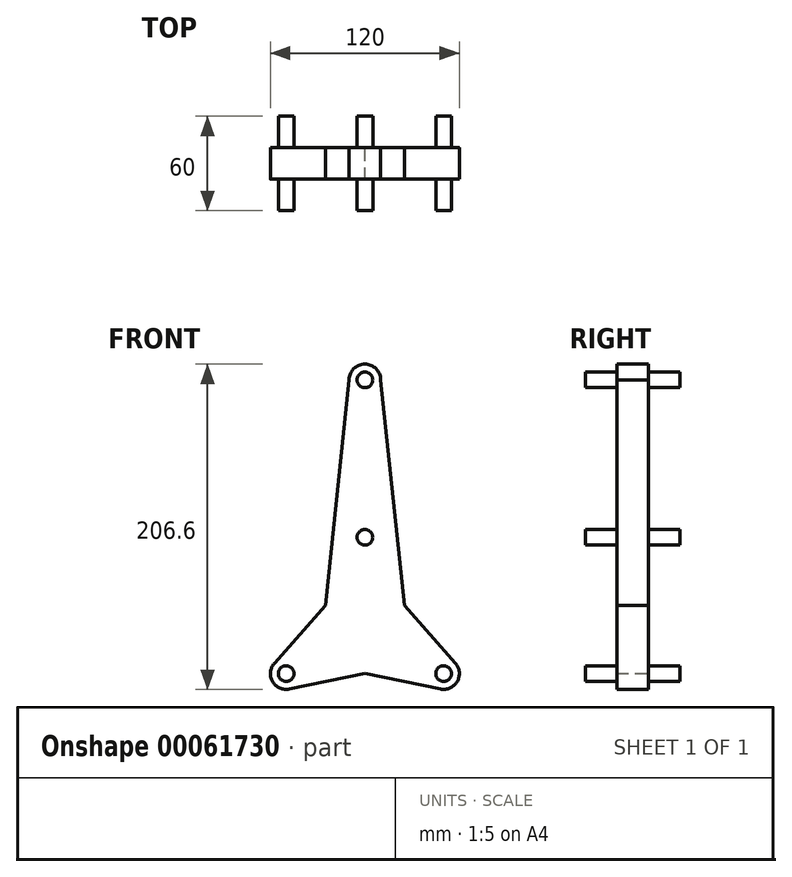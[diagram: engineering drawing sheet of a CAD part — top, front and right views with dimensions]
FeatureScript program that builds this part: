
annotation { "Feature Type Name" : "Feature", "Feature Type Description" : "" }
export const myFeature = defineFeature(function(context is Context, id is Id, definition is map)
    precondition{}
    {
        {
            var Q0;
            Q0=qCreatedBy(makeId("Front.planeOp"),FACE);
            var sketch = newSketch(context, id + "F0", { "sketchPlane" : qUnion([Q0])});
            skLineSegment(sketch, "E0", {"start": v(0, 0) * mm, "end": v(-50, -86.6) * mm});
            skLineSegment(sketch, "E1", {"start": v(-50, -86.6) * mm, "end": v(50, -86.6) * mm});
            skLineSegment(sketch, "E2", {"start": v(50, -86.6) * mm, "end": v(0, 0) * mm});
            skCircle(sketch, "E3", {"center": v(-50, -86.6) * mm, "radius": 5 * mm});
            skCircle(sketch, "E4", {"center": v(-50, -86.6) * mm, "radius": 10 * mm});
            skCircle(sketch, "E5", {"center": v(50, -86.6) * mm, "radius": 5 * mm});
            skCircle(sketch, "E6", {"center": v(50, -86.6) * mm, "radius": 10 * mm});
            skCircle(sketch, "E7", {"center": v(0, 0) * mm, "radius": 5 * mm});
            skCircle(sketch, "E8", {"center": v(0, 0) * mm, "radius": 10 * mm});
            skCircle(sketch, "E9", {"center": v(0, 100) * mm, "radius": 5 * mm});
            skCircle(sketch, "E10", {"center": v(0, 100) * mm, "radius": 10 * mm});
            skLineSegment(sketch, "E11", {"start": v(-25, -43.3) * mm, "end": v(-10, 100) * mm});
            skLineSegment(sketch, "E12", {"start": v(25, -43.3) * mm, "end": v(10, 100) * mm});
            skLineSegment(sketch, "E13", {"start": v(-25, -43.3) * mm, "end": v(-57.49, -79.97) * mm});
            skLineSegment(sketch, "E14", {"start": v(25, -43.3) * mm, "end": v(57.49, -79.97) * mm});
            skLineSegment(sketch, "E15", {"start": v(0, -86.6) * mm, "end": v(-48, -96.4) * mm});
            skLineSegment(sketch, "E16", {"start": v(0, -86.6) * mm, "end": v(48, -96.4) * mm});
            skSolve(sketch);
        }
        {
            var Q0;
            {var subQ0=sQuery(id+"F0.wireOp",EDGE,"E11");Q0=makeQuery(id+"F0.imprint","IMPRINT",FACE,{"disambiguationData":[TD([[makeQuery(id+"F0.imprint","IMPRINT",EDGE,{"derivedFrom":subQ0}),-1.0]])]});}
            var Q1;
            {var subQ0=sQuery(id+"F0.wireOp",EDGE,"E6");var subQ1=sQuery(id+"F0.wireOp",EDGE,"E1");var subQ2=makeQuery(id+"F0.imprint","INTERSECT",VERTEX,{"derivedFrom":[subQ1,subQ0]});Q1=makeQuery(id+"F0.imprint","IMPRINT",FACE,{"disambiguationData":[TD([[makeQuery(id+"F0.imprint","IMPRINT",EDGE,{"disambiguationData":[TD([[subQ2,-1.0]])],"derivedFrom":subQ1}),1.0]])]});}
            var Q2;
            {var subQ0=sQuery(id+"F0.wireOp",EDGE,"E7");var subQ1=sQuery(id+"F0.wireOp",EDGE,"E0");var subQ2=makeQuery(id+"F0.imprint","INTERSECT",VERTEX,{"derivedFrom":[subQ1,subQ0]});Q2=makeQuery(id+"F0.imprint","IMPRINT",FACE,{"disambiguationData":[TD([[makeQuery(id+"F0.imprint","IMPRINT",EDGE,{"disambiguationData":[TD([[subQ2,-1.0]])],"derivedFrom":subQ1}),-1.0]])]});}
            var Q3;
            {var subQ0=sQuery(id+"F0.wireOp",EDGE,"E13");Q3=makeQuery(id+"F0.imprint","IMPRINT",FACE,{"disambiguationData":[TD([[makeQuery(id+"F0.imprint","IMPRINT",EDGE,{"derivedFrom":subQ0}),1.0]])]});}
            var Q4;
            {var subQ3=sQuery(id+"F0.wireOp",EDGE,"E6");var subQ6=sQuery(id+"F0.wireOp",EDGE,"E1");var subQ8=makeQuery(id+"F0.imprint","INTERSECT",VERTEX,{"derivedFrom":[subQ6,subQ3]});Q4=makeQuery(id+"F0.imprint","IMPRINT",FACE,{"disambiguationData":[TD([[makeQuery(id+"F0.imprint","IMPRINT",EDGE,{"disambiguationData":[TD([[subQ8,-1.0]])],"derivedFrom":subQ6}),-1.0]])]});}
            var Q5;
            {var subQ0=sQuery(id+"F0.wireOp",EDGE,"E4");var subQ1=sQuery(id+"F0.wireOp",EDGE,"E0");var subQ2=makeQuery(id+"F0.imprint","INTERSECT",VERTEX,{"derivedFrom":[subQ1,subQ0]});Q5=makeQuery(id+"F0.imprint","IMPRINT",FACE,{"disambiguationData":[TD([[makeQuery(id+"F0.imprint","IMPRINT",EDGE,{"disambiguationData":[TD([[subQ2,-1.0]])],"derivedFrom":subQ1}),1.0]])]});}
            var Q6;
            {var subQ0=sQuery(id+"F0.wireOp",EDGE,"E15");Q6=makeQuery(id+"F0.imprint","IMPRINT",FACE,{"disambiguationData":[TD([[makeQuery(id+"F0.imprint","IMPRINT",EDGE,{"derivedFrom":subQ0}),-1.0]])]});}
            var Q7;
            {var subQ0=sQuery(id+"F0.wireOp",EDGE,"E16");Q7=makeQuery(id+"F0.imprint","IMPRINT",FACE,{"disambiguationData":[TD([[makeQuery(id+"F0.imprint","IMPRINT",EDGE,{"derivedFrom":subQ0}),1.0]])]});}
            var Q8;
            {var subQ0=sQuery(id+"F0.wireOp",EDGE,"E14");Q8=makeQuery(id+"F0.imprint","IMPRINT",FACE,{"disambiguationData":[TD([[makeQuery(id+"F0.imprint","IMPRINT",EDGE,{"derivedFrom":subQ0}),-1.0]])]});}
            var Q9;
            Q9=makeQuery(id+"F0.imprint","IMPRINT",FACE,{"disambiguationData":[TD([[makeQuery(id+"F0.imprint","IMPRINT",EDGE,{"derivedFrom":sQuery(id+"F0.wireOp",EDGE,"E9")}),-1.0]])]});
            var Q10;
            {var subQ0=sQuery(id+"F0.wireOp",EDGE,"E4");var subQ2=sQuery(id+"F0.wireOp",EDGE,"E0");var subQ3=makeQuery(id+"F0.imprint","INTERSECT",VERTEX,{"derivedFrom":[subQ2,subQ0]});Q10=makeQuery(id+"F0.imprint","IMPRINT",FACE,{"disambiguationData":[TD([[makeQuery(id+"F0.imprint","IMPRINT",EDGE,{"disambiguationData":[TD([[subQ3,-1.0]])],"derivedFrom":subQ2}),-1.0]])]});}
            var Q11;
            {var subQ4=sQuery(id+"F0.wireOp",EDGE,"E0");var subQ8=sQuery(id+"F0.wireOp",EDGE,"E4");var subQ12=makeQuery(id+"F0.imprint","INTERSECT",VERTEX,{"derivedFrom":[subQ4,subQ8]});Q11=makeQuery(id+"F0.imprint","IMPRINT",FACE,{"disambiguationData":[TD([[makeQuery(id+"F0.imprint","IMPRINT",EDGE,{"disambiguationData":[TD([[subQ12,1.0]])],"derivedFrom":subQ8}),-1.0]])]});}
            var Q12;
            {var subQ0=sQuery(id+"F0.wireOp",EDGE,"E7");var subQ1=sQuery(id+"F0.wireOp",EDGE,"E0");var subQ2=makeQuery(id+"F0.imprint","INTERSECT",VERTEX,{"derivedFrom":[subQ1,subQ0]});Q12=makeQuery(id+"F0.imprint","IMPRINT",FACE,{"disambiguationData":[TD([[makeQuery(id+"F0.imprint","IMPRINT",EDGE,{"disambiguationData":[TD([[subQ2,-1.0]])],"derivedFrom":subQ1}),1.0]])]});}
            extrude(context, id + "F1", {"entities" : qUnion([Q0, Q1, Q2, Q3, Q4, Q5, Q6, Q7, Q8, Q9, Q10, Q11, Q12]), "endBound" : BoundingType.SYMMETRIC, "depth" : 20 * mm});
        }
        {
            var Q0;
            Q0=makeQuery(id+"F0.imprint","IMPRINT",FACE,{"disambiguationData":[TD([[makeQuery(id+"F0.imprint","IMPRINT",EDGE,{"derivedFrom":sQuery(id+"F0.wireOp",EDGE,"E9")}),1.0]])]});
            var Q1;
            {var subQ0=sQuery(id+"F0.wireOp",EDGE,"E2");var subQ1=sQuery(id+"F0.wireOp",EDGE,"E0");var subQ2=makeQuery(id+"F0.imprint","INTERSECT",VERTEX,{"derivedFrom":[subQ1,subQ0]});Q1=makeQuery(id+"F0.imprint","IMPRINT",FACE,{"disambiguationData":[TD([[makeQuery(id+"F0.imprint","IMPRINT",EDGE,{"disambiguationData":[TD([[subQ2,-1.0]])],"derivedFrom":subQ1}),-1.0]])]});}
            var Q2;
            {var subQ0=sQuery(id+"F0.wireOp",EDGE,"E2");var subQ1=sQuery(id+"F0.wireOp",EDGE,"E0");var subQ2=makeQuery(id+"F0.imprint","INTERSECT",VERTEX,{"derivedFrom":[subQ1,subQ0]});Q2=makeQuery(id+"F0.imprint","IMPRINT",FACE,{"disambiguationData":[TD([[makeQuery(id+"F0.imprint","IMPRINT",EDGE,{"disambiguationData":[TD([[subQ2,-1.0]])],"derivedFrom":subQ1}),1.0]])]});}
            var Q3;
            {var subQ0=sQuery(id+"F0.wireOp",EDGE,"E1");var subQ1=sQuery(id+"F0.wireOp",EDGE,"E0");var subQ2=makeQuery(id+"F0.imprint","INTERSECT",VERTEX,{"derivedFrom":[subQ1,subQ0]});Q3=makeQuery(id+"F0.imprint","IMPRINT",FACE,{"disambiguationData":[TD([[makeQuery(id+"F0.imprint","IMPRINT",EDGE,{"disambiguationData":[TD([[subQ2,1.0]])],"derivedFrom":subQ1}),1.0]])]});}
            var Q4;
            {var subQ0=sQuery(id+"F0.wireOp",EDGE,"E1");var subQ1=sQuery(id+"F0.wireOp",EDGE,"E0");var subQ2=makeQuery(id+"F0.imprint","INTERSECT",VERTEX,{"derivedFrom":[subQ1,subQ0]});Q4=makeQuery(id+"F0.imprint","IMPRINT",FACE,{"disambiguationData":[TD([[makeQuery(id+"F0.imprint","IMPRINT",EDGE,{"disambiguationData":[TD([[subQ2,1.0]])],"derivedFrom":subQ1}),-1.0]])]});}
            var Q5;
            {var subQ0=sQuery(id+"F0.wireOp",EDGE,"E2");var subQ1=sQuery(id+"F0.wireOp",EDGE,"E1");var subQ2=makeQuery(id+"F0.imprint","INTERSECT",VERTEX,{"derivedFrom":[subQ1,subQ0]});Q5=makeQuery(id+"F0.imprint","IMPRINT",FACE,{"disambiguationData":[TD([[makeQuery(id+"F0.imprint","IMPRINT",EDGE,{"disambiguationData":[TD([[subQ2,1.0]])],"derivedFrom":subQ1}),1.0]])]});}
            var Q6;
            {var subQ0=sQuery(id+"F0.wireOp",EDGE,"E2");var subQ1=sQuery(id+"F0.wireOp",EDGE,"E1");var subQ2=makeQuery(id+"F0.imprint","INTERSECT",VERTEX,{"derivedFrom":[subQ1,subQ0]});Q6=makeQuery(id+"F0.imprint","IMPRINT",FACE,{"disambiguationData":[TD([[makeQuery(id+"F0.imprint","IMPRINT",EDGE,{"disambiguationData":[TD([[subQ2,1.0]])],"derivedFrom":subQ1}),-1.0]])]});}
            extrude(context, id + "F2", {"entities" : qUnion([Q0, Q1, Q2, Q3, Q4, Q5, Q6]), "operationType" : NewBodyOperationType.ADD, "endBound" : BoundingType.SYMMETRIC, "depth" : 60 * mm});
        }
    });
